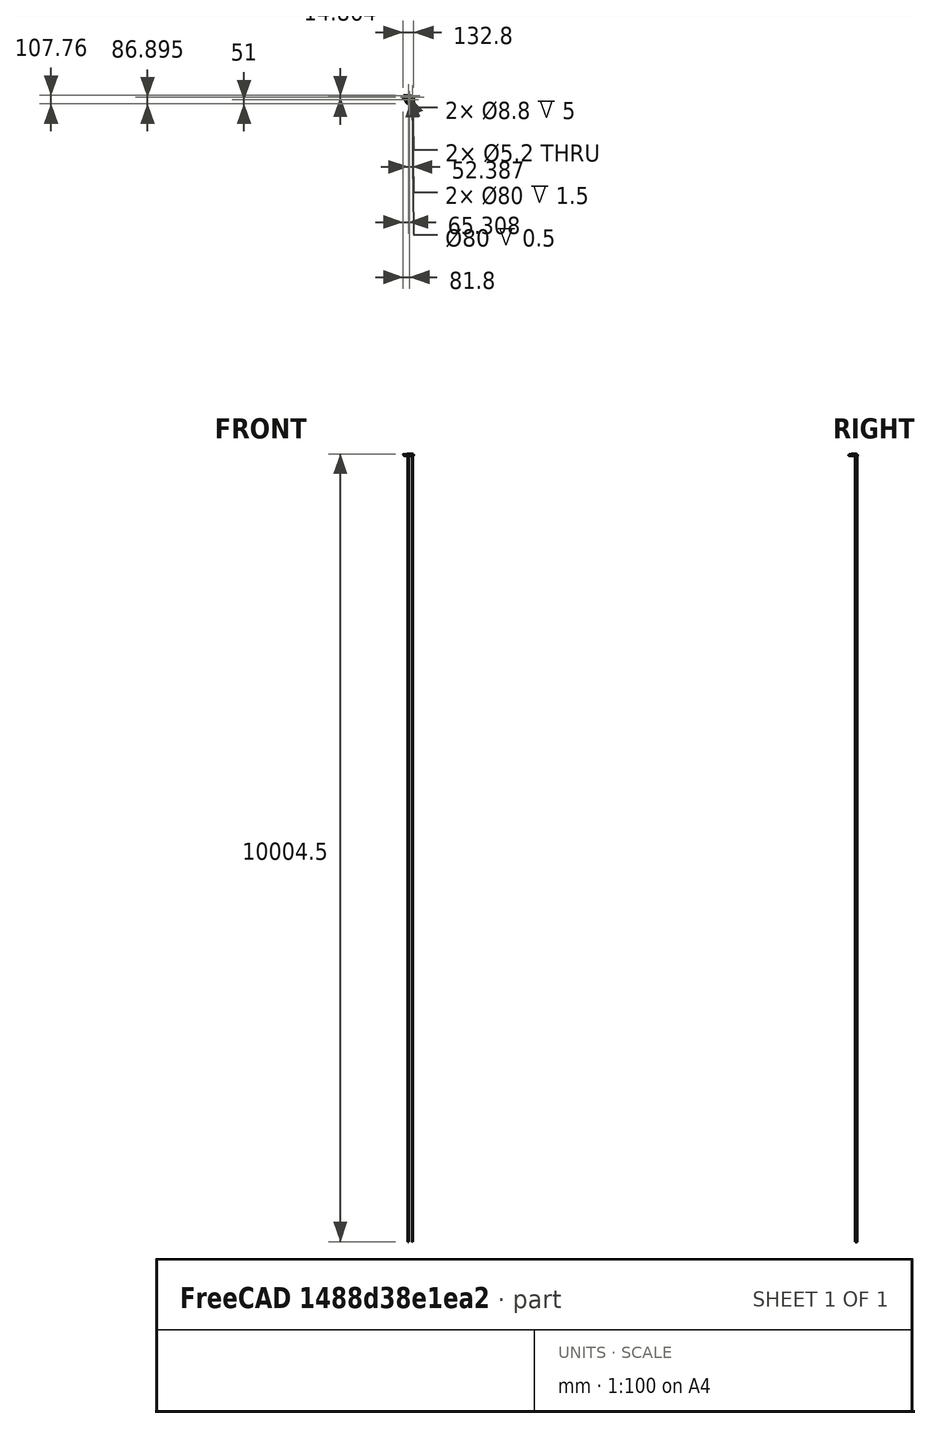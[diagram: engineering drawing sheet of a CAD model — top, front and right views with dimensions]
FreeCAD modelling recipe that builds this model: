
FCSTD DOCUMENT  (FreeCAD 0.16R)
Label: SimpleChainguard6
License: All rights reserved
LicenseURL: http://en.wikipedia.org/wiki/All_rights_reserved
objects: Sketcher::SketchObject×7, Part::Cylinder×4, PartDesign::Pad×3, PartDesign::Pocket×3, Part::Cut×2, PartDesign::Chamfer×2, PartDesign::Fillet×2, PartDesign::Revolution×1, Part::MultiFuse×1, Mesh::Feature×1
note: 32 computed .brp shape members not serialized (recipe doc carries the construction recipe); baked Part::Feature solids carry a one-line shape summary decoded from their .brp

FEATURE [Sketcher::SketchObject] Sketch
  sketch-geometry (7):
    g0: Circle CenterX=0 CenterY=0 CenterZ=0 NormalX=0 NormalY=0 NormalZ=1 Radius=40
    g1: ArcOfCircle CenterX=0 CenterY=0 CenterZ=0 NormalX=0 NormalY=0 NormalZ=1 Radius=51 StartAngle=3.54457 EndAngle=7.85398
    g2: LineSegment StartX=-75 StartY=51 StartZ=0 EndX=0 EndY=51 EndZ=0
    g3: ArcOfCircle CenterX=-54.8043 CenterY=33.0798 CenterZ=0 NormalX=0 NormalY=0 NormalZ=1 Radius=27 StartAngle=2.41582 EndAngle=4.05122
    g4: ArcOfCircle CenterX=-120.507 CenterY=-51.3726 CenterZ=0 NormalX=0 NormalY=0 NormalZ=1 Radius=80 StartAngle=0.402976 EndAngle=0.909627
    g5: LineSegment [constr] StartX=0 StartY=0 StartZ=0 EndX=114.907 EndY=96.4181 EndZ=0
    g6: LineSegment [constr] StartX=-46.3525 StartY=142.658 StartZ=0 EndX=0 EndY=0 EndZ=0
  constraints (22):
    c: Radius(g0) = 40
    c: Coincident(g0,g-1)
    c: Coincident(g1,g-1)
    c: PointOnObject(g1,g-2)
    c: Coincident(g2,g1)
    c: Horizontal(g2)
    c: Distance(g2) = 75
    c: Coincident(g3,g2)
    c: Coincident(g4,g3)
    c: Coincident(g4,g1)
    c: Tangent(g4,g3)
    c: Tangent(g1,g4)
    c: Radius(g1) = 51
    c: Radius(g4) = 80
    c: Radius(g3) = 27
    c: Coincident(g5,g-1)
    c: Angle(g6) = -1.25664
    c: Coincident(g6,g-1)
    c: Angle(g5) = 0.698132
    c: Distance(g5) = 150
    c: Distance(g6) = 150
    c: DistanceY(g1) = -20
FEATURE [PartDesign::Pad] Pad
  Length = 1.5
  Length2 = 100
  Sketch = -> Sketch
  Type = 0
FEATURE [Sketcher::SketchObject] Sketch004
  Placement = pos=(0,0,0) rot=(0.57735,0.57735,0.57735;2.0944rad)
  sketch-geometry (8):
    g0: LineSegment StartX=48.364 StartY=-12.364 StartZ=0 EndX=45.8891 EndY=-9.88909 EndZ=0
    g1: ArcOfCircle CenterX=42 CenterY=-6 CenterZ=0 NormalX=0 NormalY=0 NormalZ=1 Radius=5.5 StartAngle=5.49779 EndAngle=6.28319
    g2: ArcOfCircle CenterX=42 CenterY=-6 CenterZ=0 NormalX=0 NormalY=0 NormalZ=1 Radius=9 StartAngle=5.49779 EndAngle=6.28319
    g3: LineSegment [constr] StartX=35.4204 StartY=-25.3075 StartZ=0 EndX=48.364 EndY=-12.364 EndZ=0
    g4: LineSegment [constr] StartX=19.9837 StartY=-35.7944 StartZ=0 EndX=45.8891 EndY=-9.88909 EndZ=0
    g5: LineSegment StartX=47.5 StartY=-6 StartZ=0 EndX=47.5 EndY=0 EndZ=0
    g6: LineSegment StartX=51 StartY=-6 StartZ=0 EndX=51 EndY=0 EndZ=0
    g7: LineSegment StartX=47.5 StartY=0 StartZ=0 EndX=51 EndY=0 EndZ=0
  constraints (25):
    c: Coincident(g2,g1)
    c: Parallel(g3,g4)
    c: Angle(g4) = 0.785398
    c: Coincident(g0,g2)
    c: Coincident(g0,g1)
    c: Perpendicular(g2,g0)
    c: DistanceX(g1) = 42
    c: Distance(g3) = 18.3049
    c: Distance(g4) = 36.6357
    c: Coincident(g0,g3)
    c: Coincident(g4,g0)
    c: Tangent(g4,g1)
    c: DistanceX(g2) = 51
    c: Coincident(g5,g1)
    c: PointOnObject(g5,g-1)
    c: Coincident(g6,g2)
    c: PointOnObject(g6,g-1)
    c: Vertical(g6)
    c: Distance(g5) = 6
    c: Tangent(g1,g5)
    c: Vertical(g5)
    c: Tangent(g2,g6)
    c: Coincident(g7,g5)
    c: Coincident(g7,g6)
    c: Distance(g7) = 3.5
FEATURE [Part::Cylinder] Cylinder002
  Angle = 360
  Height = 8
  Placement = pos=(-17,27,-2) rot=(0,0,1;0rad)
  Radius = 20
FEATURE [Part::Cylinder] Cylinder003
  Angle = 360
  Height = 8
  Placement = pos=(12,12,-2) rot=(0,0,1;0rad)
  Radius = 30
FEATURE [PartDesign::Revolution] Revolution
  Angle = 180
  Axis = (0,0,1)
  Base = (0,0,0)
  Placement = pos=(0,0,0) rot=(0.57735,0.57735,0.57735;2.0944rad)
  ReferenceAxis = -> Sketch004 [V_Axis]
  Reversed = true
  Sketch = -> Sketch004
FEATURE [Sketcher::SketchObject] Sketch009
  Placement = pos=(0,0,0) rot=(0.57735,0.57735,0.57735;2.0944rad)
  sketch-geometry (8):
    g0: LineSegment StartX=48.364 StartY=-12.364 StartZ=0 EndX=45.8891 EndY=-9.88909 EndZ=0
    g1: ArcOfCircle CenterX=42 CenterY=-6 CenterZ=0 NormalX=0 NormalY=0 NormalZ=1 Radius=5.5 StartAngle=5.49779 EndAngle=6.28319
    g2: ArcOfCircle CenterX=42 CenterY=-6 CenterZ=0 NormalX=0 NormalY=0 NormalZ=1 Radius=9 StartAngle=5.49779 EndAngle=6.28319
    g3: LineSegment [constr] StartX=35.4204 StartY=-25.3075 StartZ=0 EndX=48.364 EndY=-12.364 EndZ=0
    g4: LineSegment [constr] StartX=19.9837 StartY=-35.7944 StartZ=0 EndX=45.8891 EndY=-9.88909 EndZ=0
    g5: LineSegment StartX=47.5 StartY=-6 StartZ=0 EndX=47.5 EndY=0 EndZ=0
    g6: LineSegment StartX=51 StartY=-6 StartZ=0 EndX=51 EndY=0 EndZ=0
    g7: LineSegment StartX=47.5 StartY=0 StartZ=0 EndX=51 EndY=0 EndZ=0
  constraints (25):
    c: Coincident(g2,g1)
    c: Parallel(g3,g4)
    c: Angle(g4) = 0.785398
    c: Coincident(g0,g2)
    c: Coincident(g0,g1)
    c: Perpendicular(g2,g0)
    c: DistanceX(g1) = 42
    c: Distance(g3) = 18.3049
    c: Distance(g4) = 36.6357
    c: Coincident(g0,g3)
    c: Coincident(g4,g0)
    c: Tangent(g4,g1)
    c: DistanceX(g2) = 51
    c: Coincident(g5,g1)
    c: PointOnObject(g5,g-1)
    c: Coincident(g6,g2)
    c: PointOnObject(g6,g-1)
    c: Vertical(g6)
    c: Distance(g5) = 6
    c: Tangent(g1,g5)
    c: Vertical(g5)
    c: Tangent(g2,g6)
    c: Coincident(g7,g5)
    c: Coincident(g7,g6)
    c: Distance(g7) = 3.5
FEATURE [PartDesign::Pad] Pad001
  Length = 75
  Length2 = 100
  Placement = pos=(0,0,0) rot=(0.57735,0.57735,0.57735;2.0944rad)
  Reversed = true
  Sketch = -> Sketch009
  Type = 0
FEATURE [Part::MultiFuse] Fusion
  Shapes = -> [Pad001,Revolution,Pad]
FEATURE [Sketcher::SketchObject] Sketch005
  Placement = pos=(0,0,1.5) rot=(0,0,1;0rad)
  Support = -> Fusion [Face5]
  sketch-geometry (4):
    g0: LineSegment [constr] StartX=-45.1089 StartY=138.831 StartZ=0 EndX=0 EndY=0 EndZ=0
    g1: LineSegment [constr] StartX=122.75 StartY=122.75 StartZ=0 EndX=0 EndY=0 EndZ=0
    g2: Circle CenterX=-16.4924 CenterY=50.7583 CenterZ=0 NormalX=0 NormalY=0 NormalZ=1 Radius=6
    g3: Circle CenterX=35.8947 CenterY=35.8947 CenterZ=0 NormalX=0 NormalY=0 NormalZ=1 Radius=6
  constraints (8):
    c: Coincident(g0,g-1)
    c: Coincident(g1,g-1)
    c: Angle(g1) = -2.35619
    c: Angle(g0) = -1.25664
    c: Radius(g2) = 6
    c: PointOnObject(g2,g0)
    c: Radius(g3) = 6
    c: PointOnObject(g3,g1)
FEATURE [PartDesign::Pad] Pad002
  Length = 21
  Length2 = 100
  Reversed = true
  Sketch = -> Sketch005
  Type = 0
FEATURE [Sketcher::SketchObject] Sketch012
  ExternalGeometry = -> [Pad002]
  Placement = pos=(0,0,1.5) rot=(0,0,1;0rad)
  Support = -> Pad002 [Face5]
  sketch-geometry (2):
    g0: Circle CenterX=-16.4924 CenterY=50.7583 CenterZ=0 NormalX=0 NormalY=0 NormalZ=1 Radius=2.6
    g1: Circle CenterX=35.8947 CenterY=35.8947 CenterZ=0 NormalX=0 NormalY=0 NormalZ=1 Radius=2.6
  constraints (4):
    c: Radius(g1) = 2.6
    c: Equal(g1,g0)
    c: Coincident(g0,g-3)
    c: Coincident(g1,g-4)
FEATURE [PartDesign::Pocket] Pocket
  Length = 5
  Sketch = -> Sketch012
  Type = 1
FEATURE [Sketcher::SketchObject] Sketch013
  ExternalGeometry = -> [Pocket]
  Placement = pos=(0,0,1.5) rot=(0,0,1;0rad)
  Support = -> Pocket [Face5]
  sketch-geometry (2):
    g0: Circle CenterX=-16.4924 CenterY=50.7583 CenterZ=0 NormalX=0 NormalY=0 NormalZ=1 Radius=4.4
    g1: Circle CenterX=35.8947 CenterY=35.8947 CenterZ=0 NormalX=0 NormalY=0 NormalZ=1 Radius=4.4
  constraints (4):
    c: Radius(g0) = 4.4
    c: Equal(g0,g1)
    c: Coincident(g1,g-4)
    c: Coincident(g0,g-3)
FEATURE [PartDesign::Pocket] Pocket001
  Length = 5
  Sketch = -> Sketch013
  Type = 0
FEATURE [Sketcher::SketchObject] Sketch008
  Placement = pos=(0,0,-19.5) rot=(1,0,0;3.14159rad)
  Support = -> Pocket001 [Face39]
  sketch-geometry (4):
    g0: LineSegment StartX=-35.7258 StartY=-32.8433 StartZ=0 EndX=0 EndY=-32.8433 EndZ=0
    g1: LineSegment StartX=0 StartY=-32.8433 StartZ=0 EndX=0 EndY=-68.5691 EndZ=0
    g2: LineSegment StartX=0 StartY=-68.5691 StartZ=0 EndX=-35.7258 EndY=-68.5691 EndZ=0
    g3: LineSegment StartX=-35.7258 StartY=-68.5691 StartZ=0 EndX=-35.7258 EndY=-32.8433 EndZ=0
  constraints (12):
    c: Coincident(g0,g1)
    c: Coincident(g1,g2)
    c: Coincident(g2,g3)
    c: Coincident(g3,g0)
    c: Horizontal(g0)
    c: Horizontal(g2)
    c: Vertical(g1)
    c: Vertical(g3)
    c: PointOnObject(g1,g-2)
    c: Equal(g0,g1)
    c: Distance(g1) = 35.7258
    c: DistanceY(g0) = -32.8433
FEATURE [PartDesign::Pocket] Pocket002
  Length = 1.5
  Sketch = -> Sketch008
  Type = 0
FEATURE [Part::Cylinder] Cylinder
  Angle = 360
  Height = 8
  Placement = pos=(0,0,-9) rot=(0,0,1;0rad)
  Radius = 46
FEATURE [Part::Cut] Cut
  Base = -> Pocket002
  Tool = -> Cylinder
FEATURE [Part::Cylinder] Cylinder004
  Angle = 360
  Height = 8
  Placement = pos=(-17,-1.8,-9) rot=(0,0,1;0rad)
  Radius = 48
FEATURE [Part::Cut] Cut001
  Base = -> Cut
  Tool = -> Cylinder004
FEATURE [PartDesign::Chamfer] Chamfer
  Base = -> Cut001 [Edge27]
  Size = 1
FEATURE [PartDesign::Chamfer] Chamfer001
  Base = -> Chamfer [Edge4]
  Size = 1
FEATURE [PartDesign::Fillet] Fillet
  Base = -> Chamfer001 [Edge124,Edge72]
  Radius = 4
FEATURE [PartDesign::Fillet] Fillet001
  Base = -> Fillet [Edge29,Edge83]
  Radius = 1
FEATURE [Mesh::Feature] Mesh  label="Fillet001 (Meshed)"
